# Revit family: ARX.4-P-D
name_source: partatom
category: Lighting Fixtures
revit_build: Autodesk Revit 2018 (Build: 20170223_1515(x64)
units: mm (PartAtom-declared; Revit-internal decimal feet)

## family parameters
Cut with Voids When Loaded = No
Host = Face
Light Source = Yes
Part Type = Normal
Room Calculation Point = Yes
Round Connector Dimension = Use Diameter
Shared = Yes

## types (7) — shared parameters
Color Filter = 16777215
Default Elevation = 4' - 0"
Dimming Lamp Color Temperature Shift = <None>
Emit Shape Visible in Rendering = No
Emit from Rectangle Width = 0' - 3"
Fixture Symbol Visiblity = Yes
Fixture Width = 0' - 4 1/2"
Lamp = LED
Photometric Web File = ARX_4-P-D-375-4-40K-8.ies
Switch Leg Visibility = No
Tilt Angle = 90.00°

## per-type parameters (varying)
| type | Apparent Load | Emit from Rectangle Length | Fixture Length | Manufacturer | Type Comments | Voltage |
| 2' Direct | 6 VA | 2' - 0" | 2' - 0" |  | LUX ILLUMINAIRE | 120 V |
| 3' Direct | 9 VA | 3' - 0" | 3' - 0" |  | LUX ILLUMINAIRE | 0 V |
| 4' Direct | 12 VA | 4' - 0" | 4' - 0" |  | LUX ILLUMINAIRE | 0 V |
| 5' Direct | 16 VA | 5' - 0" | 5' - 0" |  | LUX ILLUMINAIRE | 0 V |
| 6' Direct | 19 VA | 6' - 0" | 6' - 0" | LUX ILLUMINAIRE |  | 0 V |
| 7' Direct | 22 VA | 7' - 0" | 7' - 0" | LUX ILLUMINAIRE |  | 0 V |
| 8' Direct | 25 VA | 8' - 0" | 8' - 0" | LUX ILLUMINAIRE |  | 0 V |

## geometry (parser evidence)
native form markers: Sweep x3
no freeform markers — native parametric forms only
